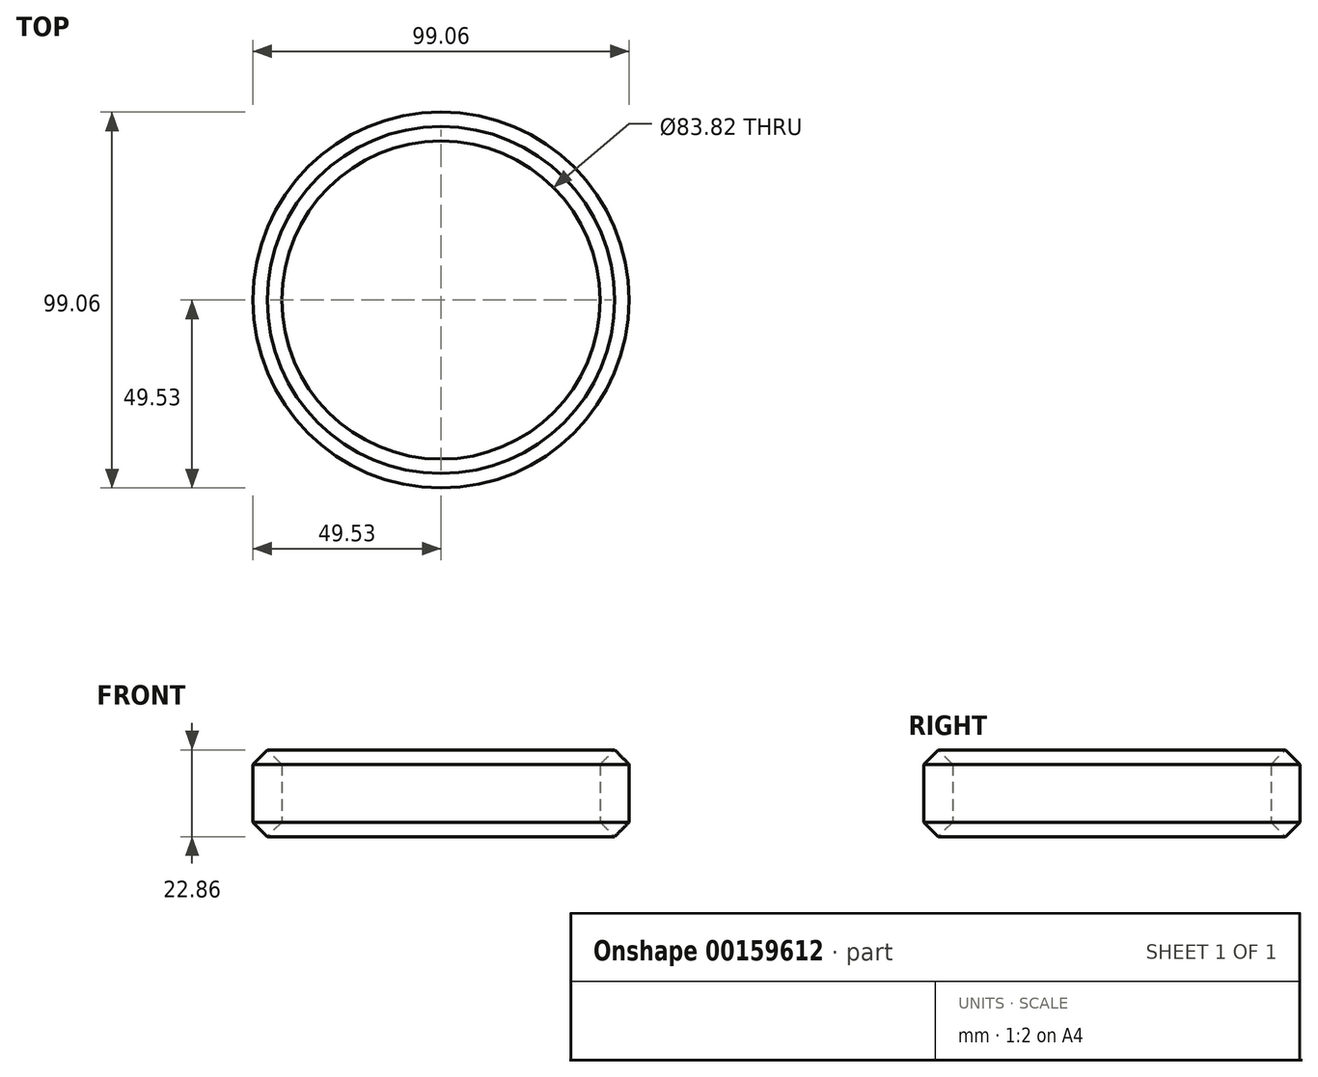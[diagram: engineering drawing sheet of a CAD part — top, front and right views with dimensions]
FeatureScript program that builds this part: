
annotation { "Feature Type Name" : "Feature", "Feature Type Description" : "" }
export const myFeature = defineFeature(function(context is Context, id is Id, definition is map)
    precondition{}
    {
        {
            var Q0;
            Q0=qCreatedBy(makeId("Top.planeOp"),FACE);
            var sketch = newSketch(context, id + "F0", { "sketchPlane" : qUnion([Q0])});
            skCircle(sketch, "E0", {"center": v(0, 0) * mm, "radius": 49.53 * mm});
            skCircle(sketch, "E1", {"center": v(0, 0) * mm, "radius": 41.91 * mm});
            skSolve(sketch);
        }
        {
            var Q0;
            Q0 = qSketchRegion(id + "F0", true);
            extrude(context, id + "F1", {"entities" : qUnion([Q0]), "depth" : 25.4 * mm});
        }
        {
            var Q0;
            Q0=makeQuery(id+"F1.opExtrude","CAP_EDGE",EDGE,{"disambiguationData":[OSD([sQuery(id+"F0.wireOp",EDGE,"E1")])],"isStart":false});
            chamfer(context, id + "F2", {"entities" : qUnion([Q0]), "width" : 5.08 * mm, "tangentPropagation" : true});
        }
        {
            var Q0;
            Q0=makeQuery(id+"F1.opExtrude","CAP_EDGE",EDGE,{"disambiguationData":[OSD([sQuery(id+"F0.wireOp",EDGE,"E0")])],"isStart":false});
            chamfer(context, id + "F3", {"entities" : qUnion([Q0]), "width" : 5.08 * mm, "tangentPropagation" : true});
        }
        {
            var Q0;
            Q0=makeQuery(id+"F1.opExtrude","CAP_EDGE",EDGE,{"disambiguationData":[OSD([sQuery(id+"F0.wireOp",EDGE,"E0")])],"isStart":true});
            chamfer(context, id + "F4", {"entities" : qUnion([Q0]), "width" : 5.08 * mm, "tangentPropagation" : true});
        }
        {
            var Q0;
            Q0=makeQuery(id+"F1.opExtrude","CAP_EDGE",EDGE,{"disambiguationData":[OSD([sQuery(id+"F0.wireOp",EDGE,"E1")])],"isStart":true});
            chamfer(context, id + "F5", {"entities" : qUnion([Q0]), "width" : 5.08 * mm, "tangentPropagation" : true});
        }
    });
